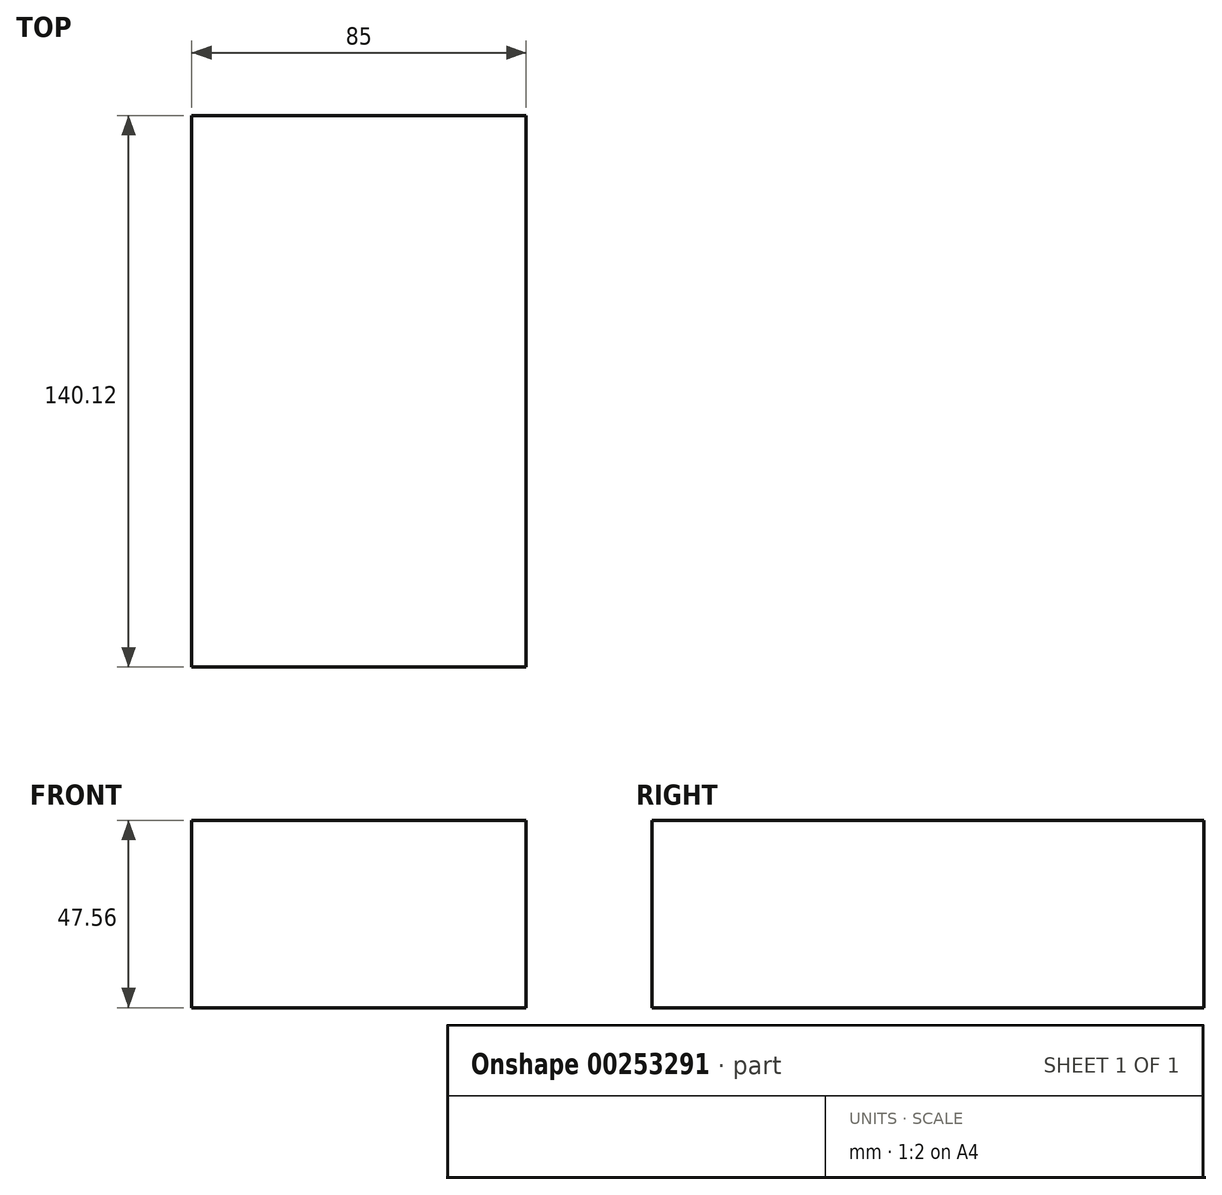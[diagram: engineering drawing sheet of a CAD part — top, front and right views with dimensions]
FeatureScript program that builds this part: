
annotation { "Feature Type Name" : "Feature", "Feature Type Description" : "" }
export const myFeature = defineFeature(function(context is Context, id is Id, definition is map)
    precondition{}
    {
        {
            var Q0;
            Q0=qCreatedBy(makeId("Right.planeOp"),FACE);
            var sketch = newSketch(context, id + "F0", { "sketchPlane" : qUnion([Q0])});
            skLineSegment(sketch, "E0.bottom", {"start": v(-70.06, 23.78) * mm, "end": v(70.06, 23.78) * mm});
            skLineSegment(sketch, "E0.top", {"start": v(-70.06, -23.78) * mm, "end": v(70.06, -23.78) * mm});
            skLineSegment(sketch, "E0.left", {"start": v(-70.06, 23.78) * mm, "end": v(-70.06, -23.78) * mm});
            skLineSegment(sketch, "E0.right", {"start": v(70.06, 23.78) * mm, "end": v(70.06, -23.78) * mm});
            skPoint(sketch, "E0.middle", {"position": v(0, 0) * mm});
            skSolve(sketch);
        }
        {
            var Q0;
            Q0=makeQuery(id+"F0.imprint","IMPRINT",FACE,{"disambiguationData":[TD([[makeQuery(id+"F0.imprint","IMPRINT",EDGE,{"derivedFrom":sQuery(id+"F0.wireOp",EDGE,"E0.bottom")}),-1.0]])]});
            extrude(context, id + "F1", {"entities" : qUnion([Q0]), "depth" : 85 * mm});
        }
    });
